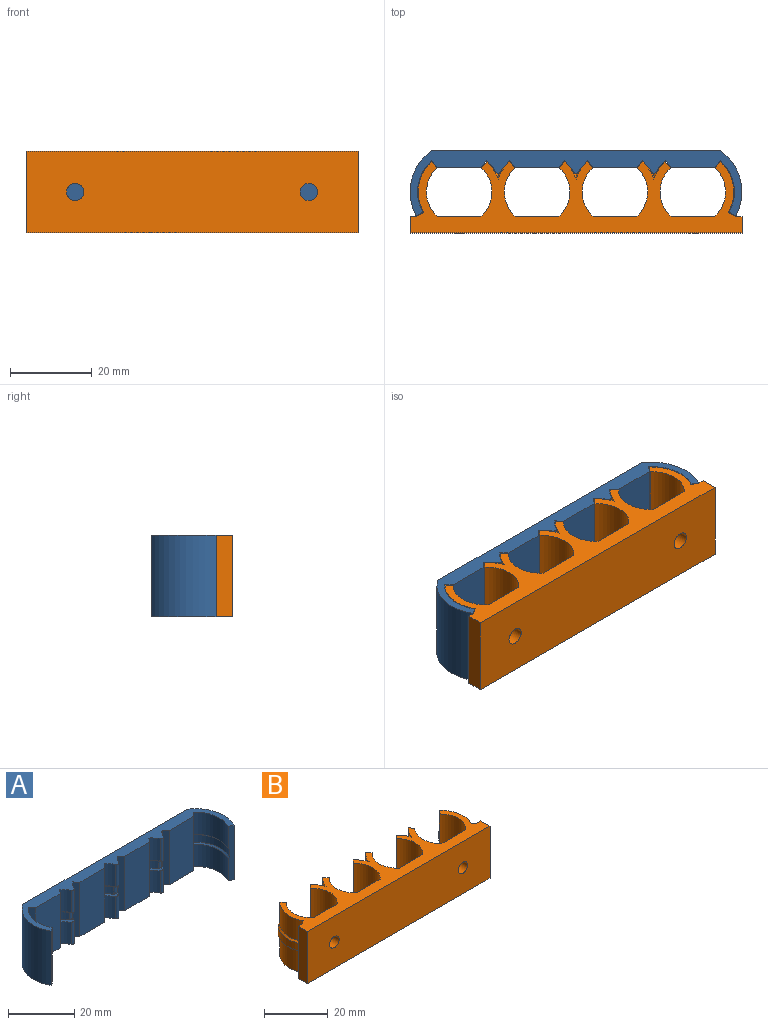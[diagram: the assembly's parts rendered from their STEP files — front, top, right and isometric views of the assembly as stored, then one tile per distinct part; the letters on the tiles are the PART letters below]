
ASSEMBLY  parts=2 mates=1
PART A: 68 faces, bbox 81x15.9x20 mm
  f0: plane 81x15.87mm, normal (0,0,1), area 330.6mm2, adj f1,f2,f3,f4,f5,f6,f7,f10
  f1: cylinder r=12mm len=20mm, axis (0,0,-1), area 359.1mm2, adj f0,f5,f39,f42
  f2: plane 20x10.58mm, normal (0,-1,0), area 211.7mm2, adj f0,f35,f37,f42
  f3: plane 20x10.58mm, normal (0,-1,0), area 211.7mm2, adj f0,f28,f36,f42
  f4: plane 20x10.58mm, normal (0,-1,0), area 211.7mm2, adj f0,f20,f27,f42
  f5: plane 70.27x20mm, normal (0,1,0), area 1405.3mm2, adj f0,f1,f7,f42
  f6: plane 20x10.58mm, normal (0,-1,0), area 211.7mm2, adj f0,f12,f19,f42
  f7: cylinder r=12mm len=20mm, axis (0,0,-1), area 359.1mm2, adj f0,f5,f11,f42
  f8: cone r=10.6mm half-angle=45deg, axis (0,0,-1), area 9mm2, adj f9,f10,f11,f12
  f9: cylinder r=10.6mm len=13.12mm, axis (0,0,-1), area 40.3mm2, adj f8,f11,f12,f43
  f10: cylinder r=10.15mm len=12.56mm, axis (0,0,-1), area 112.2mm2, adj f0,f8,f11,f12
  f11: plane 20x1.6mm, normal (-0.5,-0.87,0), area 35.5mm2, adj f0,f7,f8,f9,f10,f42,f43,f44
  f12: plane 20x1.95mm, normal (0.75,-0.66,0), area 44.5mm2, adj f0,f6,f8,f9,f10,f42,f43,f44
  f13: cone r=10.6mm half-angle=45deg, axis (0,0,-1), area 2.8mm2, adj f14,f16,f18,f20,f66,f67
  f14: cone r=10.6mm half-angle=45deg, axis (0,0,-1), area 2.8mm2, adj f13,f15,f17,f19,f66,f67
  f15: cylinder r=10.15mm len=8.15mm, axis (0,0,-1), area 28.4mm2, adj f0,f14,f19,f66
  f16: cylinder r=10.15mm len=8.15mm, axis (0,0,-1), area 28.4mm2, adj f0,f13,f20,f66
  f17: cylinder r=10.6mm len=2.8mm, axis (0,0,-1), area 8.2mm2, adj f14,f19,f46,f67
  f18: cylinder r=10.6mm len=2.8mm, axis (0,0,-1), area 8.2mm2, adj f13,f20,f45,f67
  f19: plane 20x1.95mm, normal (-0.75,-0.66,0), area 44.5mm2, adj f0,f6,f14,f15,f17,f42,f46,f47
  f20: plane 20x1.95mm, normal (0.75,-0.66,0), area 44.5mm2, adj f0,f4,f13,f16,f18,f42,f45,f48
  f21: cone r=10.6mm half-angle=45deg, axis (0,0,-1), area 2.8mm2, adj f22,f24,f26,f28,f64,f65
  f22: cone r=10.6mm half-angle=45deg, axis (0,0,-1), area 2.8mm2, adj f21,f23,f25,f27,f64,f65
  f23: cylinder r=10.15mm len=8.15mm, axis (0,0,-1), area 28.4mm2, adj f0,f22,f27,f64
  f24: cylinder r=10.15mm len=8.15mm, axis (0,0,-1), area 28.4mm2, adj f0,f21,f28,f64
  f25: cylinder r=10.6mm len=2.8mm, axis (0,0,-1), area 8.2mm2, adj f22,f27,f50,f65
  f26: cylinder r=10.6mm len=2.8mm, axis (0,0,-1), area 8.2mm2, adj f21,f28,f49,f65
  f27: plane 20x1.95mm, normal (-0.75,-0.66,0), area 44.5mm2, adj f0,f4,f22,f23,f25,f42,f50,f51
  f28: plane 20x1.95mm, normal (0.75,-0.66,0), area 44.5mm2, adj f0,f3,f21,f24,f26,f42,f49,f52
  f29: cone r=10.6mm half-angle=45deg, axis (0,0,-1), area 2.8mm2, adj f30,f32,f34,f35,f62,f63
  f30: cone r=10.6mm half-angle=45deg, axis (0,0,-1), area 2.8mm2, adj f29,f31,f33,f36,f62,f63
  f31: cylinder r=10.15mm len=8.15mm, axis (0,0,-1), area 28.4mm2, adj f0,f30,f36,f62
  f32: cylinder r=10.15mm len=8.15mm, axis (0,0,-1), area 28.4mm2, adj f0,f29,f35,f62
  f33: cylinder r=10.6mm len=2.8mm, axis (0,0,-1), area 8.2mm2, adj f30,f36,f54,f63
  f34: cylinder r=10.6mm len=2.8mm, axis (0,0,-1), area 8.2mm2, adj f29,f35,f53,f63
  f35: plane 20x1.95mm, normal (0.75,-0.66,0), area 44.5mm2, adj f0,f2,f29,f32,f34,f42,f53,f56
  f36: plane 20x1.95mm, normal (-0.75,-0.66,0), area 44.5mm2, adj f0,f3,f30,f31,f33,f42,f54,f55
  f37: plane 20x1.95mm, normal (-0.75,-0.66,0), area 44.5mm2, adj f0,f2,f38,f40,f41,f42,f57,f58
  f38: cylinder r=10.15mm len=12.56mm, axis (0,0,-1), area 112.2mm2, adj f0,f37,f39,f41
  f39: plane 20x1.6mm, normal (0.5,-0.87,0), area 35.5mm2, adj f0,f1,f38,f40,f41,f42,f57,f58
  f40: cylinder r=10.6mm len=13.12mm, axis (0,0,-1), area 40.3mm2, adj f37,f39,f41,f58
  f41: cone r=10.6mm half-angle=45deg, axis (0,0,-1), area 9mm2, adj f37,f38,f39,f40
  f42: plane 81x15.87mm, normal (0,0,-1), area 330.6mm2, adj f1,f2,f3,f4,f5,f6,f7,f11
  f43: cone r=10.6mm half-angle=45deg, axis (0,0,1), area 9mm2, adj f9,f11,f12,f44
  f44: cylinder r=10.15mm len=12.56mm, axis (0,0,1), area 112.2mm2, adj f11,f12,f42,f43
  f45: cone r=10.6mm half-angle=45deg, axis (0,0,1), area 2.8mm2, adj f18,f20,f46,f48,f61,f67
  f46: cone r=10.6mm half-angle=45deg, axis (0,0,1), area 2.8mm2, adj f17,f19,f45,f47,f61,f67
  f47: cylinder r=10.15mm len=8.15mm, axis (0,0,1), area 28.4mm2, adj f19,f42,f46,f61
  f48: cylinder r=10.15mm len=8.15mm, axis (0,0,1), area 28.4mm2, adj f20,f42,f45,f61
  f49: cone r=10.6mm half-angle=45deg, axis (0,0,1), area 2.8mm2, adj f26,f28,f50,f52,f59,f65
  f50: cone r=10.6mm half-angle=45deg, axis (0,0,1), area 2.8mm2, adj f25,f27,f49,f51,f59,f65
  f51: cylinder r=10.15mm len=8.15mm, axis (0,0,1), area 28.4mm2, adj f27,f42,f50,f59
  f52: cylinder r=10.15mm len=8.15mm, axis (0,0,1), area 28.4mm2, adj f28,f42,f49,f59
  f53: cone r=10.6mm half-angle=45deg, axis (0,0,1), area 2.8mm2, adj f34,f35,f54,f56,f60,f63
  f54: cone r=10.6mm half-angle=45deg, axis (0,0,1), area 2.8mm2, adj f33,f36,f53,f55,f60,f63
  f55: cylinder r=10.15mm len=8.15mm, axis (0,0,1), area 28.4mm2, adj f36,f42,f54,f60
  f56: cylinder r=10.15mm len=8.15mm, axis (0,0,1), area 28.4mm2, adj f35,f42,f53,f60
  f57: cylinder r=10.15mm len=12.56mm, axis (0,0,1), area 112.2mm2, adj f37,f39,f42,f58
  f58: cone r=10.6mm half-angle=45deg, axis (0,0,1), area 9mm2, adj f37,f39,f40,f57
  f59: cylinder r=0.7mm len=8.53mm, axis (0,0,-1), area 12.4mm2, adj f42,f49,f50,f51,f52
  f60: cylinder r=0.7mm len=8.53mm, axis (0,0,-1), area 12.4mm2, adj f42,f53,f54,f55,f56
  f61: cylinder r=0.7mm len=8.53mm, axis (0,0,-1), area 12.4mm2, adj f42,f45,f46,f47,f48
  f62: cylinder r=0.7mm len=8.53mm, axis (0,0,1), area 12.4mm2, adj f0,f29,f30,f31,f32
  f63: cylinder r=0.7mm len=2.8mm, axis (0,0,1), area 3.6mm2, adj f29,f30,f33,f34,f53,f54
  f64: cylinder r=0.7mm len=8.53mm, axis (0,0,1), area 12.4mm2, adj f0,f21,f22,f23,f24
  f65: cylinder r=0.7mm len=2.8mm, axis (0,0,1), area 3.6mm2, adj f21,f22,f25,f26,f49,f50
  f66: cylinder r=0.7mm len=8.53mm, axis (0,0,1), area 12.4mm2, adj f0,f13,f14,f15,f16
  f67: cylinder r=0.7mm len=2.8mm, axis (0,0,1), area 3.6mm2, adj f13,f14,f17,f18,f45,f46
PART B: 71 faces, bbox 81x17.8x20 mm
  f0: cylinder r=8mm len=20mm, axis (0,0,-1), area 267.4mm2, adj f1,f6,f45,f52
  f1: plane 81x17.37mm, normal (0,0,1), area 549.3mm2, adj f0,f2,f3,f4,f5,f6,f7,f8
  f2: plane 20x4mm, normal (-1,0,0), area 80mm2, adj f1,f3,f4,f52
  f3: plane 81x20mm, normal (0,-1,0), area 1592.3mm2, adj f1,f2,f15,f52,f69,f70
  f4: plane 20x1.61mm, normal (0,1,0), area 32.2mm2, adj f1,f2,f49,f52
  f5: cylinder r=8mm len=20mm, axis (0,0,-1), area 267.4mm2, adj f1,f6,f47,f52
  f6: plane 20x10.58mm, normal (0,1,0), area 197.8mm2, adj f0,f1,f5,f52,f70
  f7: cylinder r=8mm len=20mm, axis (0,0,-1), area 267.4mm2, adj f1,f9,f46,f52
  f8: cylinder r=8mm len=20mm, axis (0,0,-1), area 267.4mm2, adj f1,f9,f38,f52
  f9: plane 20x10.58mm, normal (0,1,0), area 211.7mm2, adj f1,f7,f8,f52
  f10: cylinder r=8mm len=20mm, axis (0,0,-1), area 267.4mm2, adj f1,f12,f37,f52
  f11: cylinder r=8mm len=20mm, axis (0,0,-1), area 267.4mm2, adj f1,f12,f30,f52
  f12: plane 20x10.58mm, normal (0,1,0), area 211.7mm2, adj f1,f10,f11,f52
  f13: cylinder r=8mm len=20mm, axis (0,0,-1), area 267.4mm2, adj f1,f14,f29,f52
  f14: plane 20x10.58mm, normal (0,1,0), area 197.8mm2, adj f1,f13,f17,f52,f69
  f15: plane 20x4mm, normal (1,0,0), area 80mm2, adj f1,f3,f16,f52
  f16: plane 20x1.61mm, normal (0,1,0), area 32.2mm2, adj f1,f15,f21,f52
  f17: cylinder r=8mm len=20mm, axis (0,0,-1), area 267.4mm2, adj f1,f14,f22,f52
  f18: cone r=10.6mm half-angle=45deg, axis (0,0,-1), area 11.8mm2, adj f19,f20,f21,f22
  f19: cylinder r=10.6mm len=13.12mm, axis (0,0,-1), area 40.2mm2, adj f18,f21,f22,f53
  f20: cylinder r=10mm len=12.37mm, axis (0,0,-1), area 108.1mm2, adj f1,f18,f21,f22
  f21: plane 20x1.73mm, normal (0.5,0.87,0), area 38mm2, adj f1,f16,f18,f19,f20,f52,f53,f54
  f22: plane 20x1.95mm, normal (-0.75,0.66,0), area 42.1mm2, adj f1,f17,f18,f19,f20,f52,f53,f54
  f23: cone r=10.6mm half-angle=45deg, axis (0,0,-1), area 3.8mm2, adj f24,f26,f28,f30
  f24: cone r=10.6mm half-angle=45deg, axis (0,0,-1), area 3.8mm2, adj f23,f25,f27,f29
  f25: cylinder r=10mm len=8mm, axis (0,0,-1), area 40.8mm2, adj f1,f24,f26,f29
  f26: cylinder r=10mm len=8mm, axis (0,0,-1), area 40.8mm2, adj f1,f23,f25,f30
  f27: cylinder r=10.6mm len=3.11mm, axis (0,0,-1), area 11mm2, adj f24,f28,f29,f56
  f28: cylinder r=10.6mm len=3.11mm, axis (0,0,-1), area 11mm2, adj f23,f27,f30,f55
  f29: plane 20x1.95mm, normal (0.75,0.66,0), area 42.1mm2, adj f1,f13,f24,f25,f27,f52,f56,f57
  f30: plane 20x1.95mm, normal (-0.75,0.66,0), area 42.1mm2, adj f1,f11,f23,f26,f28,f52,f55,f58
  f31: cone r=10.6mm half-angle=45deg, axis (0,0,-1), area 3.8mm2, adj f32,f34,f36,f38
  f32: cone r=10.6mm half-angle=45deg, axis (0,0,-1), area 3.8mm2, adj f31,f33,f35,f37
  f33: cylinder r=10mm len=8mm, axis (0,0,-1), area 40.8mm2, adj f1,f32,f34,f37
  f34: cylinder r=10mm len=8mm, axis (0,0,-1), area 40.8mm2, adj f1,f31,f33,f38
  f35: cylinder r=10.6mm len=3.11mm, axis (0,0,-1), area 11mm2, adj f32,f36,f37,f60
  f36: cylinder r=10.6mm len=3.11mm, axis (0,0,-1), area 11mm2, adj f31,f35,f38,f59
  f37: plane 20x1.95mm, normal (0.75,0.66,0), area 42.1mm2, adj f1,f10,f32,f33,f35,f52,f60,f61
  f38: plane 20x1.95mm, normal (-0.75,0.66,0), area 42.1mm2, adj f1,f8,f31,f34,f36,f52,f59,f62
  f39: cone r=10.6mm half-angle=45deg, axis (0,0,-1), area 3.8mm2, adj f40,f42,f44,f45
  f40: cone r=10.6mm half-angle=45deg, axis (0,0,-1), area 3.8mm2, adj f39,f41,f43,f46
  f41: cylinder r=10mm len=8mm, axis (0,0,-1), area 40.8mm2, adj f1,f40,f42,f46
  f42: cylinder r=10mm len=8mm, axis (0,0,-1), area 40.8mm2, adj f1,f39,f41,f45
  f43: cylinder r=10.6mm len=3.11mm, axis (0,0,-1), area 11mm2, adj f40,f44,f46,f64
  f44: cylinder r=10.6mm len=3.11mm, axis (0,0,-1), area 11mm2, adj f39,f43,f45,f63
  f45: plane 20x1.95mm, normal (-0.75,0.66,0), area 42.1mm2, adj f0,f1,f39,f42,f44,f52,f63,f66
  f46: plane 20x1.95mm, normal (0.75,0.66,0), area 42.1mm2, adj f1,f7,f40,f41,f43,f52,f64,f65
  f47: plane 20x1.95mm, normal (0.75,0.66,0), area 42.1mm2, adj f1,f5,f48,f50,f51,f52,f67,f68
  f48: cylinder r=10mm len=12.37mm, axis (0,0,-1), area 108.1mm2, adj f1,f47,f49,f51
  f49: plane 20x1.73mm, normal (-0.5,0.87,0), area 38mm2, adj f1,f4,f48,f50,f51,f52,f67,f68
  f50: cylinder r=10.6mm len=13.12mm, axis (0,0,-1), area 40.2mm2, adj f47,f49,f51,f68
  f51: cone r=10.6mm half-angle=45deg, axis (0,0,-1), area 11.8mm2, adj f47,f48,f49,f50
  f52: plane 81x17.37mm, normal (0,0,-1), area 549.3mm2, adj f0,f2,f3,f4,f5,f6,f7,f8
  f53: cone r=10.6mm half-angle=45deg, axis (0,0,1), area 11.8mm2, adj f19,f21,f22,f54
  f54: cylinder r=10mm len=12.37mm, axis (0,0,1), area 108.1mm2, adj f21,f22,f52,f53
  f55: cone r=10.6mm half-angle=45deg, axis (0,0,1), area 3.8mm2, adj f28,f30,f56,f58
  f56: cone r=10.6mm half-angle=45deg, axis (0,0,1), area 3.8mm2, adj f27,f29,f55,f57
  f57: cylinder r=10mm len=8mm, axis (0,0,1), area 40.8mm2, adj f29,f52,f56,f58
  f58: cylinder r=10mm len=8mm, axis (0,0,1), area 40.8mm2, adj f30,f52,f55,f57
  f59: cone r=10.6mm half-angle=45deg, axis (0,0,1), area 3.8mm2, adj f36,f38,f60,f62
  f60: cone r=10.6mm half-angle=45deg, axis (0,0,1), area 3.8mm2, adj f35,f37,f59,f61
  f61: cylinder r=10mm len=8mm, axis (0,0,1), area 40.8mm2, adj f37,f52,f60,f62
  f62: cylinder r=10mm len=8mm, axis (0,0,1), area 40.8mm2, adj f38,f52,f59,f61
  f63: cone r=10.6mm half-angle=45deg, axis (0,0,1), area 3.8mm2, adj f44,f45,f64,f66
  f64: cone r=10.6mm half-angle=45deg, axis (0,0,1), area 3.8mm2, adj f43,f46,f63,f65
  f65: cylinder r=10mm len=8mm, axis (0,0,1), area 40.8mm2, adj f46,f52,f64,f66
  f66: cylinder r=10mm len=8mm, axis (0,0,1), area 40.8mm2, adj f45,f52,f63,f65
  f67: cylinder r=10mm len=12.37mm, axis (0,0,1), area 108.1mm2, adj f47,f49,f52,f68
  f68: cone r=10.6mm half-angle=45deg, axis (0,0,1), area 11.8mm2, adj f47,f49,f50,f67
  f69: cylinder r=2.1mm len=4.2mm, axis (0,-1,0), area 52.8mm2, adj f3,f14
  f70: cylinder r=2.1mm len=4.2mm, axis (0,-1,0), area 52.8mm2, adj f3,f6
PLACE A t=(-34.36,-2.78,-8.96)mm
PLACE B t=(-34.36,-2.78,-8.96)mm
MATE fastened A.f38 <-> B.f5  axis (0,0,1) through (-34.36,-2.78,1.04)mm
